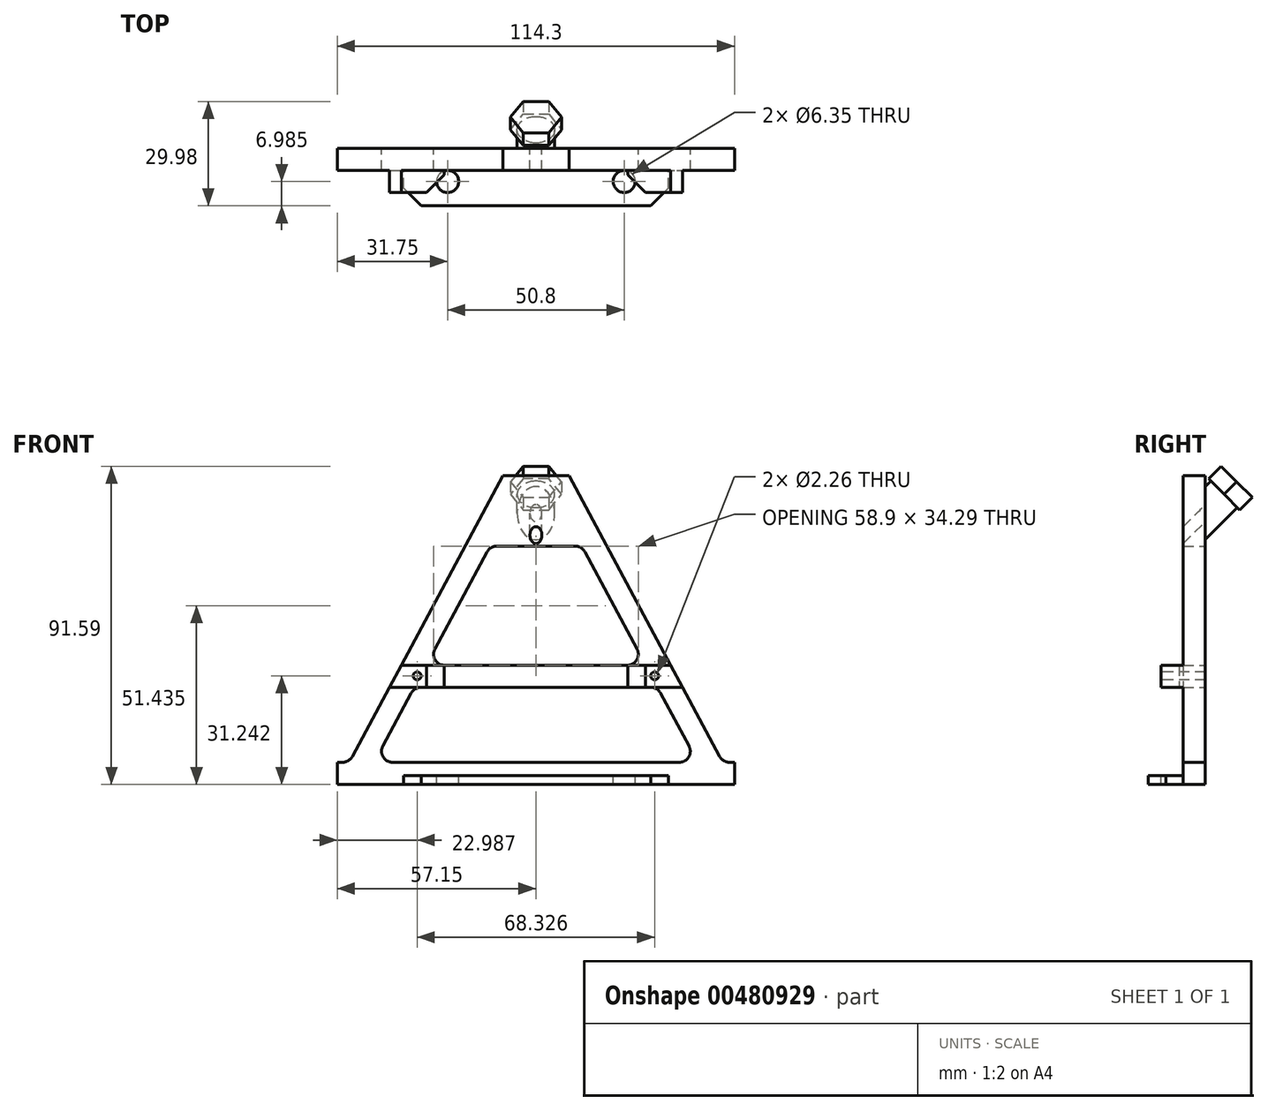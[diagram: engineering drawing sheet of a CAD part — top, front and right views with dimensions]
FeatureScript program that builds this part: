
annotation { "Feature Type Name" : "Feature", "Feature Type Description" : "" }
export const myFeature = defineFeature(function(context is Context, id is Id, definition is map)
    precondition{}
    {
        {
            var Q0;
            Q0=qCreatedBy(makeId("Front.planeOp"),FACE);
            var sketch = newSketch(context, id + "F0", { "sketchPlane" : qUnion([Q0])});
            skLineSegment(sketch, "E0", {"start": v(-9.53, 88.9) * mm, "end": v(9.52, 88.9) * mm});
            skLineSegment(sketch, "E1", {"start": v(-57.15, 0) * mm, "end": v(57.15, 0) * mm});
            skLineSegment(sketch, "E2", {"start": v(57.15, 0) * mm, "end": v(-57.15, 0) * mm});
            skLineSegment(sketch, "E3", {"start": v(-9.52, 88.9) * mm, "end": v(-57.15, 0) * mm});
            skLineSegment(sketch, "E4", {"start": v(9.52, 88.9) * mm, "end": v(57.15, 0) * mm});
            skLineSegment(sketch, "E5", {"start": v(-57.15, 0) * mm, "end": v(-57.15, 6.35) * mm});
            skLineSegment(sketch, "E6", {"start": v(-41.24, 6.35) * mm, "end": v(41.24, 6.35) * mm});
            skLineSegment(sketch, "E7", {"start": v(57.15, 6.35) * mm, "end": v(57.15, 0) * mm});
            skLineSegment(sketch, "E8", {"start": v(-44.04, 11.02) * mm, "end": v(-35.88, 26.26) * mm});
            skLineSegment(sketch, "E9", {"start": v(-11.3, 68.58) * mm, "end": v(11.3, 68.58) * mm});
            skLineSegment(sketch, "E10", {"start": v(35.88, 26.26) * mm, "end": v(44.04, 11.02) * mm});
            skLineSegment(sketch, "E11", {"start": v(-33.08, 27.94) * mm, "end": v(33.08, 27.94) * mm});
            skLineSegment(sketch, "E12", {"start": v(-26.27, 34.3) * mm, "end": v(26.27, 34.3) * mm});
            skArc(sketch, "E13.filletArc", {"start": v(35.88, 26.26) * mm, "mid": v(34.7, 27.49) * mm, "end": v(33.08, 27.94) * mm});
            skArc(sketch, "E14.filletArc", {"start": v(-33.08, 27.94) * mm, "mid": v(-34.7, 27.49) * mm, "end": v(-35.88, 26.26) * mm});
            skArc(sketch, "E15.filletArc", {"start": v(-44.04, 11.02) * mm, "mid": v(-43.97, 7.9) * mm, "end": v(-41.24, 6.35) * mm});
            skPoint(sketch, "E16.newPointA", {"position": v(57.15, 6.35) * mm});
            skArc(sketch, "E16.filletArc", {"start": v(41.24, 6.35) * mm, "mid": v(43.97, 7.9) * mm, "end": v(44.04, 11.02) * mm});
            skLineSegment(sketch, "E17", {"start": v(-29.07, 38.96) * mm, "end": v(-14.1, 66.9) * mm});
            skLineSegment(sketch, "E18", {"start": v(14.1, 66.9) * mm, "end": v(29.07, 38.96) * mm});
            skLineSegment(sketch, "E19", {"start": v(-57.15, 6.35) * mm, "end": v(-53.75, 6.35) * mm});
            skLineSegment(sketch, "E20.trimOffspring", {"start": v(53.75, 6.35) * mm, "end": v(57.15, 6.35) * mm});
            skPoint(sketch, "E21.visualSharp", {"position": v(-31.58, 34.3) * mm});
            skArc(sketch, "E21.filletArc", {"start": v(-29.07, 38.96) * mm, "mid": v(-29, 35.83) * mm, "end": v(-26.27, 34.3) * mm});
            skPoint(sketch, "E22.visualSharp", {"position": v(31.58, 34.3) * mm});
            skArc(sketch, "E22.filletArc", {"start": v(26.27, 34.3) * mm, "mid": v(29, 35.83) * mm, "end": v(29.07, 38.96) * mm});
            skPoint(sketch, "E23.visualSharp", {"position": v(13.2, 68.58) * mm});
            skArc(sketch, "E23.filletArc", {"start": v(14.1, 66.9) * mm, "mid": v(12.94, 68.13) * mm, "end": v(11.3, 68.58) * mm});
            skPoint(sketch, "E24.visualSharp", {"position": v(-13.2, 68.58) * mm});
            skArc(sketch, "E24.filletArc", {"start": v(-11.3, 68.58) * mm, "mid": v(-12.94, 68.13) * mm, "end": v(-14.1, 66.9) * mm});
            skSolve(sketch);
        }
        {
            var Q0;
            Q0 = qSketchRegion(id + "F0", true);
            extrude(context, id + "F1", {"entities" : qUnion([Q0]), "depth" : 6.35 * mm});
        }
        {
            var Q0;
            Q0=makeQuery(id+"F1.opExtrude","SWEPT_EDGE",EDGE,{"disambiguationData":[OSD([sQuery(id+"F0.wireOp",EDGE,"E4"),sQuery(id+"F0.wireOp",EDGE,"E20.trimOffspring")])]});
            var Q1;
            Q1=makeQuery(id+"F1.opExtrude","SWEPT_EDGE",EDGE,{"disambiguationData":[OSD([sQuery(id+"F0.wireOp",EDGE,"E3"),sQuery(id+"F0.wireOp",EDGE,"E19")])]});
            fillet(context, id + "F2", {"entities" : qUnion([Q0, Q1]), "radius" : 3.17 * mm, "tangentPropagation" : true, "allowEdgeOverflow" : false});
        }
        {
            var Q0;
            Q0=makeQuery(id+"F1.opExtrude","CAP_FACE",FACE,{"disambiguationData":[OSD([sQuery(id+"F0.wireOp",EDGE,"E0"),sQuery(id+"F0.wireOp",EDGE,"E2"),sQuery(id+"F0.wireOp",EDGE,"E3"),sQuery(id+"F0.wireOp",EDGE,"E4"),sQuery(id+"F0.wireOp",EDGE,"E5"),sQuery(id+"F0.wireOp",EDGE,"E7"),sQuery(id+"F0.wireOp",EDGE,"E8"),sQuery(id+"F0.wireOp",EDGE,"E9"),sQuery(id+"F0.wireOp",EDGE,"E10"),sQuery(id+"F0.wireOp",EDGE,"E11"),sQuery(id+"F0.wireOp",EDGE,"E12"),sQuery(id+"F0.wireOp",EDGE,"E13.filletArc"),sQuery(id+"F0.wireOp",EDGE,"E14.filletArc"),sQuery(id+"F0.wireOp",EDGE,"E15.filletArc"),sQuery(id+"F0.wireOp",EDGE,"E16.filletArc"),sQuery(id+"F0.wireOp",EDGE,"E17"),sQuery(id+"F0.wireOp",EDGE,"E18"),sQuery(id+"F0.wireOp",EDGE,"E19"),sQuery(id+"F0.wireOp",EDGE,"E6"),sQuery(id+"F0.wireOp",EDGE,"E20.trimOffspring"),sQuery(id+"F0.wireOp",EDGE,"E21.filletArc"),sQuery(id+"F0.wireOp",EDGE,"E22.filletArc"),sQuery(id+"F0.wireOp",EDGE,"E23.filletArc"),sQuery(id+"F0.wireOp",EDGE,"E24.filletArc")])],"isStart":false});
            var sketch = newSketch(context, id + "F3", { "sketchPlane" : qUnion([Q0])});
            skLineSegment(sketch, "E25.bottom", {"start": v(-38.1, 0) * mm, "end": v(38.1, 0) * mm});
            skLineSegment(sketch, "E25.top", {"start": v(-38.1, 2.54) * mm, "end": v(38.1, 2.54) * mm});
            skLineSegment(sketch, "E25.left", {"start": v(-38.1, 0) * mm, "end": v(-38.1, 2.54) * mm});
            skLineSegment(sketch, "E25.right", {"start": v(38.1, 0) * mm, "end": v(38.1, 2.54) * mm});
            skSolve(sketch);
        }
        {
            var Q0;
            Q0 = qSketchRegion(id + "F3", true);
            extrude(context, id + "F4", {"entities" : qUnion([Q0]), "operationType" : NewBodyOperationType.ADD, "depth" : 10.16 * mm});
        }
        {
            var Q0;
            Q0=makeQuery(id+"F4.opExtrude","CAP_EDGE",EDGE,{"disambiguationData":[OSD([sQuery(id+"F3.wireOp",EDGE,"E25.left")])],"isStart":false});
            var Q1;
            Q1=makeQuery(id+"F4.opExtrude","CAP_EDGE",EDGE,{"disambiguationData":[OSD([sQuery(id+"F3.wireOp",EDGE,"E25.right")])],"isStart":false});
            chamfer(context, id + "F5", {"entities" : qUnion([Q0, Q1]), "width" : 5.08 * mm, "tangentPropagation" : true});
        }
        {
            var Q0;
            Q0=makeQuery(id+"F1.opExtrude","CAP_FACE",FACE,{"disambiguationData":[OSD([sQuery(id+"F0.wireOp",EDGE,"E0"),sQuery(id+"F0.wireOp",EDGE,"E2"),sQuery(id+"F0.wireOp",EDGE,"E3"),sQuery(id+"F0.wireOp",EDGE,"E4"),sQuery(id+"F0.wireOp",EDGE,"E5"),sQuery(id+"F0.wireOp",EDGE,"E7"),sQuery(id+"F0.wireOp",EDGE,"E8"),sQuery(id+"F0.wireOp",EDGE,"E9"),sQuery(id+"F0.wireOp",EDGE,"E10"),sQuery(id+"F0.wireOp",EDGE,"E11"),sQuery(id+"F0.wireOp",EDGE,"E12"),sQuery(id+"F0.wireOp",EDGE,"E13.filletArc"),sQuery(id+"F0.wireOp",EDGE,"E14.filletArc"),sQuery(id+"F0.wireOp",EDGE,"E15.filletArc"),sQuery(id+"F0.wireOp",EDGE,"E16.filletArc"),sQuery(id+"F0.wireOp",EDGE,"E17"),sQuery(id+"F0.wireOp",EDGE,"E18"),sQuery(id+"F0.wireOp",EDGE,"E19"),sQuery(id+"F0.wireOp",EDGE,"E6"),sQuery(id+"F0.wireOp",EDGE,"E20.trimOffspring"),sQuery(id+"F0.wireOp",EDGE,"E21.filletArc"),sQuery(id+"F0.wireOp",EDGE,"E22.filletArc"),sQuery(id+"F0.wireOp",EDGE,"E23.filletArc"),sQuery(id+"F0.wireOp",EDGE,"E24.filletArc")])],"isStart":false});
            var sketch = newSketch(context, id + "F6", { "sketchPlane" : qUnion([Q0])});
            skLineSegment(sketch, "E26.0", {"start": v(-33.08, 27.94) * mm, "end": v(33.08, 27.94) * mm});
            skLineSegment(sketch, "E27.0", {"start": v(-26.27, 34.3) * mm, "end": v(26.27, 34.3) * mm});
            skLineSegment(sketch, "E28", {"start": v(26.27, 34.3) * mm, "end": v(38.78, 34.3) * mm});
            skLineSegment(sketch, "E29", {"start": v(33.08, 27.94) * mm, "end": v(42.18, 27.94) * mm});
            skLineSegment(sketch, "E30", {"start": v(-26.27, 34.3) * mm, "end": v(-38.78, 34.3) * mm});
            skLineSegment(sketch, "E31", {"start": v(-42.18, 27.94) * mm, "end": v(-33.08, 27.94) * mm});
            skLineSegment(sketch, "E32", {"start": v(-42.18, 27.94) * mm, "end": v(-38.78, 34.3) * mm});
            skLineSegment(sketch, "E33", {"start": v(42.18, 27.94) * mm, "end": v(38.78, 34.3) * mm});
            skLineSegment(sketch, "E34", {"start": v(26.43, 34.3) * mm, "end": v(26.43, 27.94) * mm});
            skLineSegment(sketch, "E35", {"start": v(-26.43, 34.3) * mm, "end": v(-26.43, 27.94) * mm});
            skSolve(sketch);
        }
        {
            var Q0;
            {var subQ0=sQuery(id+"F6.wireOp",EDGE,"E31");Q0=makeQuery(id+"F6.imprint","IMPRINT",FACE,{"disambiguationData":[TD([[makeQuery(id+"F6.imprint","IMPRINT",EDGE,{"derivedFrom":subQ0}),1.0]])]});}
            var Q1;
            {var subQ1=sQuery(id+"F6.wireOp",EDGE,"E29");Q1=makeQuery(id+"F6.imprint","IMPRINT",FACE,{"disambiguationData":[TD([[makeQuery(id+"F6.imprint","IMPRINT",EDGE,{"derivedFrom":subQ1}),1.0]])]});}
            extrude(context, id + "F7", {"entities" : qUnion([Q0, Q1]), "operationType" : NewBodyOperationType.ADD, "depth" : 6.35 * mm});
        }
        {
            var Q0;
            Q0=makeQuery(id+"F7.opExtrude","CAP_EDGE",EDGE,{"disambiguationData":[OSD([sQuery(id+"F6.wireOp",EDGE,"E34")])],"isStart":false});
            var Q1;
            Q1=makeQuery(id+"F7.opExtrude","CAP_EDGE",EDGE,{"disambiguationData":[OSD([sQuery(id+"F6.wireOp",EDGE,"E35")])],"isStart":false});
            chamfer(context, id + "F8", {"entities" : qUnion([Q0, Q1]), "width" : 5.08 * mm, "tangentPropagation" : true});
        }
        {
            var Q0;
            Q0=makeQuery(id+"F7.opExtrude","CAP_FACE",FACE,{"disambiguationData":[OSD([sQuery(id+"F6.wireOp",EDGE,"E26.0"),sQuery(id+"F6.wireOp",EDGE,"E28"),sQuery(id+"F6.wireOp",EDGE,"E29"),sQuery(id+"F6.wireOp",EDGE,"E33"),sQuery(id+"F6.wireOp",EDGE,"E34")])],"isStart":false});
            var sketch = newSketch(context, id + "F9", { "sketchPlane" : qUnion([Q0])});
            skPoint(sketch, "E36", {"position": v(34.16, 31.24) * mm});
            skPoint(sketch, "E37", {"position": v(-34.16, 31.24) * mm});
            skSolve(sketch);
        }
        {
            var Q0;
            Q0=sQuery(id+"F9.wireOp",VERTEX,"E37");
            var Q1;
            Q1=sQuery(id+"F9.wireOp",VERTEX,"E36");
            var Q2;
            Q2=makeQuery(id+"F1.opExtrude","SWEPT_BODY",BODY,{"disambiguationData":[OSD([sQuery(id+"F0.wireOp",EDGE,"E0"),sQuery(id+"F0.wireOp",EDGE,"E2"),sQuery(id+"F0.wireOp",EDGE,"E3"),sQuery(id+"F0.wireOp",EDGE,"E4"),sQuery(id+"F0.wireOp",EDGE,"E5"),sQuery(id+"F0.wireOp",EDGE,"E7"),sQuery(id+"F0.wireOp",EDGE,"E8"),sQuery(id+"F0.wireOp",EDGE,"E9"),sQuery(id+"F0.wireOp",EDGE,"E10"),sQuery(id+"F0.wireOp",EDGE,"E11"),sQuery(id+"F0.wireOp",EDGE,"E12"),sQuery(id+"F0.wireOp",EDGE,"E13.filletArc"),sQuery(id+"F0.wireOp",EDGE,"E14.filletArc"),sQuery(id+"F0.wireOp",EDGE,"E15.filletArc"),sQuery(id+"F0.wireOp",EDGE,"E16.filletArc"),sQuery(id+"F0.wireOp",EDGE,"E17"),sQuery(id+"F0.wireOp",EDGE,"E18"),sQuery(id+"F0.wireOp",EDGE,"E19"),sQuery(id+"F0.wireOp",EDGE,"E6"),sQuery(id+"F0.wireOp",EDGE,"E20.trimOffspring"),sQuery(id+"F0.wireOp",EDGE,"E21.filletArc"),sQuery(id+"F0.wireOp",EDGE,"E22.filletArc"),sQuery(id+"F0.wireOp",EDGE,"E23.filletArc"),sQuery(id+"F0.wireOp",EDGE,"E24.filletArc")])]});
            hole(context, id + "F10", {"style" : HoleStyle.SIMPLE, "endStyle" : HoleEndStyle.THROUGH, "standardTappedOrClearance" : lookupTablePath({ "standard" : "ANSI", "fit" : "Normal (ASME)", "engagement" : "75%", "pitch" : "40 tpi", "size" : "#4", "type" : "Tapped" }), "standardBlindInLast" : lookupTablePath({ "fit" : "Free", "standard" : "ANSI", "engagement" : "75%", "pitch" : "40 tpi", "size" : "#4", "type" : "Tapped" }), "holeDiameter" : 2.26 * mm, "showTappedDepth" : true, "tappedDepth" : 6.35 * mm, "tapClearance" : 3, "locations" : qUnion([Q0, Q1]), "scope" : qUnion([Q2]), "majorDiameter" : 2.84 * mm});
        }
        {
            var Q0;
            Q0=makeQuery(id+"F1.opExtrude","CAP_EDGE",EDGE,{"disambiguationData":[OSD([sQuery(id+"F0.wireOp",EDGE,"E0")])],"isStart":true});
            cPlane(context, id + "F11", {"entities" : qUnion([Q0]), "cplaneType" : CPlaneType.LINE_ANGLE, "offset" : 25.4 * mm, "angle" : 45 * degree, "width" : 152.4 * mm, "height" : 152.4 * mm});
        }
        {
            var Q0;
            Q0=qCreatedBy(id+"F11.planeOp",FACE);
            var sketch = newSketch(context, id + "F12", { "sketchPlane" : qUnion([Q0])});
            skCircle(sketch, "E38.cCircle", {"center": v(0, 55.24) * mm, "radius": 6.35 * mm, "construction": true});
            skLineSegment(sketch, "E38.0", {"start": v(3.67, 48.9) * mm, "end": v(-3.67, 48.9) * mm});
            skLineSegment(sketch, "E38.1", {"start": v(-3.67, 48.9) * mm, "end": v(-7.33, 55.24) * mm});
            skLineSegment(sketch, "E38.2", {"start": v(-7.33, 55.24) * mm, "end": v(-3.67, 61.6) * mm});
            skLineSegment(sketch, "E38.3", {"start": v(-3.67, 61.6) * mm, "end": v(3.67, 61.6) * mm});
            skLineSegment(sketch, "E38.4", {"start": v(3.67, 61.6) * mm, "end": v(7.33, 55.24) * mm});
            skLineSegment(sketch, "E38.5", {"start": v(7.33, 55.24) * mm, "end": v(3.67, 48.9) * mm});
            skPoint(sketch, "E38.0.midPoint", {"position": v(0, 48.9) * mm});
            skSolve(sketch);
        }
        {
            var Q0;
            Q0 = qSketchRegion(id + "F12", true);
            extrude(context, id + "F13", {"entities" : qUnion([Q0]), "depth" : 5.08 * mm});
        }
        {
            var Q0;
            Q0=makeQuery(id+"F13.opExtrude","CAP_FACE",FACE,{"disambiguationData":[OSD([sQuery(id+"F12.wireOp",EDGE,"E38.0"),sQuery(id+"F12.wireOp",EDGE,"E38.1"),sQuery(id+"F12.wireOp",EDGE,"E38.2"),sQuery(id+"F12.wireOp",EDGE,"E38.3"),sQuery(id+"F12.wireOp",EDGE,"E38.4"),sQuery(id+"F12.wireOp",EDGE,"E38.5")])],"isStart":true});
            var sketch = newSketch(context, id + "F14", { "sketchPlane" : qUnion([Q0])});
            skCircle(sketch, "E39", {"center": v(0, 55.24) * mm, "radius": 5.4 * mm});
            skSolve(sketch);
        }
        {
            var Q0;
            Q0 = qSketchRegion(id + "F14", true);
            var Q1;
            Q1=makeQuery(id+"F1.opExtrude","CAP_FACE",FACE,{"disambiguationData":[OSD([sQuery(id+"F0.wireOp",EDGE,"E0"),sQuery(id+"F0.wireOp",EDGE,"E2"),sQuery(id+"F0.wireOp",EDGE,"E3"),sQuery(id+"F0.wireOp",EDGE,"E4"),sQuery(id+"F0.wireOp",EDGE,"E5"),sQuery(id+"F0.wireOp",EDGE,"E7"),sQuery(id+"F0.wireOp",EDGE,"E8"),sQuery(id+"F0.wireOp",EDGE,"E9"),sQuery(id+"F0.wireOp",EDGE,"E10"),sQuery(id+"F0.wireOp",EDGE,"E11"),sQuery(id+"F0.wireOp",EDGE,"E12"),sQuery(id+"F0.wireOp",EDGE,"E13.filletArc"),sQuery(id+"F0.wireOp",EDGE,"E14.filletArc"),sQuery(id+"F0.wireOp",EDGE,"E15.filletArc"),sQuery(id+"F0.wireOp",EDGE,"E16.filletArc"),sQuery(id+"F0.wireOp",EDGE,"E17"),sQuery(id+"F0.wireOp",EDGE,"E18"),sQuery(id+"F0.wireOp",EDGE,"E19"),sQuery(id+"F0.wireOp",EDGE,"E6"),sQuery(id+"F0.wireOp",EDGE,"E20.trimOffspring"),sQuery(id+"F0.wireOp",EDGE,"E21.filletArc"),sQuery(id+"F0.wireOp",EDGE,"E22.filletArc"),sQuery(id+"F0.wireOp",EDGE,"E23.filletArc"),sQuery(id+"F0.wireOp",EDGE,"E24.filletArc")])],"isStart":true});
            extrude(context, id + "F15", {"entities" : qUnion([Q0]), "endBound" : BoundingType.UP_TO_SURFACE, "endBoundEntityFace" : qUnion([Q1]), "depth" : 25.4 * mm});
        }
        {
            var Q0;
            Q0=makeQuery(id+"F13.opExtrude","CAP_FACE",FACE,{"disambiguationData":[OSD([sQuery(id+"F12.wireOp",EDGE,"E38.0"),sQuery(id+"F12.wireOp",EDGE,"E38.1"),sQuery(id+"F12.wireOp",EDGE,"E38.2"),sQuery(id+"F12.wireOp",EDGE,"E38.3"),sQuery(id+"F12.wireOp",EDGE,"E38.4"),sQuery(id+"F12.wireOp",EDGE,"E38.5")])],"isStart":false});
            var sketch = newSketch(context, id + "F16", { "sketchPlane" : qUnion([Q0])});
            skPoint(sketch, "E40", {"position": v(0, 55.24) * mm});
            skSolve(sketch);
        }
        {
            var Q0;
            Q0=sQuery(id+"F16.wireOp",VERTEX,"E40");
            var Q1;
            Q1=makeQuery(id+"F1.opExtrude","SWEPT_BODY",BODY,{"disambiguationData":[OSD([sQuery(id+"F0.wireOp",EDGE,"E0"),sQuery(id+"F0.wireOp",EDGE,"E2"),sQuery(id+"F0.wireOp",EDGE,"E3"),sQuery(id+"F0.wireOp",EDGE,"E4"),sQuery(id+"F0.wireOp",EDGE,"E5"),sQuery(id+"F0.wireOp",EDGE,"E7"),sQuery(id+"F0.wireOp",EDGE,"E8"),sQuery(id+"F0.wireOp",EDGE,"E9"),sQuery(id+"F0.wireOp",EDGE,"E10"),sQuery(id+"F0.wireOp",EDGE,"E11"),sQuery(id+"F0.wireOp",EDGE,"E12"),sQuery(id+"F0.wireOp",EDGE,"E13.filletArc"),sQuery(id+"F0.wireOp",EDGE,"E14.filletArc"),sQuery(id+"F0.wireOp",EDGE,"E15.filletArc"),sQuery(id+"F0.wireOp",EDGE,"E16.filletArc"),sQuery(id+"F0.wireOp",EDGE,"E17"),sQuery(id+"F0.wireOp",EDGE,"E18"),sQuery(id+"F0.wireOp",EDGE,"E19"),sQuery(id+"F0.wireOp",EDGE,"E6"),sQuery(id+"F0.wireOp",EDGE,"E20.trimOffspring"),sQuery(id+"F0.wireOp",EDGE,"E21.filletArc"),sQuery(id+"F0.wireOp",EDGE,"E22.filletArc"),sQuery(id+"F0.wireOp",EDGE,"E23.filletArc"),sQuery(id+"F0.wireOp",EDGE,"E24.filletArc")])]});
            hole(context, id + "F17", {"style" : HoleStyle.SIMPLE, "endStyle" : HoleEndStyle.THROUGH, "standardTappedOrClearance" : lookupTablePath({ "standard" : "ANSI", "fit" : "Normal (ASME)", "engagement" : "75%", "pitch" : "32 tpi", "size" : "#8", "type" : "Tapped" }), "standardBlindInLast" : lookupTablePath({ "fit" : "Free", "standard" : "ANSI", "engagement" : "75%", "pitch" : "32 tpi", "size" : "#8", "type" : "Tapped" }), "holeDiameter" : 3.45 * mm, "showTappedDepth" : true, "tappedDepth" : 6.35 * mm, "tapClearance" : 3, "locations" : qUnion([Q0]), "scope" : qUnion([Q1]), "majorDiameter" : 4.17 * mm});
        }
        {
            var Q0;
            Q0=makeQuery(id+"F4.opExtrude","SWEPT_FACE",FACE,{"disambiguationData":[OSD([sQuery(id+"F3.wireOp",EDGE,"E25.top")])]});
            var sketch = newSketch(context, id + "F18", { "sketchPlane" : qUnion([Q0])});
            skPoint(sketch, "E41", {"position": v(-25.4, -9.53) * mm});
            skPoint(sketch, "E42", {"position": v(25.4, -9.52) * mm});
            skSolve(sketch);
        }
        {
            var Q0;
            Q0=sQuery(id+"F18.wireOp",VERTEX,"E41");
            var Q1;
            Q1=sQuery(id+"F18.wireOp",VERTEX,"E42");
            var Q2;
            Q2=makeQuery(id+"F1.opExtrude","SWEPT_BODY",BODY,{"disambiguationData":[OSD([sQuery(id+"F0.wireOp",EDGE,"E0"),sQuery(id+"F0.wireOp",EDGE,"E2"),sQuery(id+"F0.wireOp",EDGE,"E3"),sQuery(id+"F0.wireOp",EDGE,"E4"),sQuery(id+"F0.wireOp",EDGE,"E5"),sQuery(id+"F0.wireOp",EDGE,"E7"),sQuery(id+"F0.wireOp",EDGE,"E8"),sQuery(id+"F0.wireOp",EDGE,"E9"),sQuery(id+"F0.wireOp",EDGE,"E10"),sQuery(id+"F0.wireOp",EDGE,"E11"),sQuery(id+"F0.wireOp",EDGE,"E12"),sQuery(id+"F0.wireOp",EDGE,"E13.filletArc"),sQuery(id+"F0.wireOp",EDGE,"E14.filletArc"),sQuery(id+"F0.wireOp",EDGE,"E15.filletArc"),sQuery(id+"F0.wireOp",EDGE,"E16.filletArc"),sQuery(id+"F0.wireOp",EDGE,"E17"),sQuery(id+"F0.wireOp",EDGE,"E18"),sQuery(id+"F0.wireOp",EDGE,"E19"),sQuery(id+"F0.wireOp",EDGE,"E6"),sQuery(id+"F0.wireOp",EDGE,"E20.trimOffspring"),sQuery(id+"F0.wireOp",EDGE,"E21.filletArc"),sQuery(id+"F0.wireOp",EDGE,"E22.filletArc"),sQuery(id+"F0.wireOp",EDGE,"E23.filletArc"),sQuery(id+"F0.wireOp",EDGE,"E24.filletArc")])]});
            hole(context, id + "F19", {"style" : HoleStyle.SIMPLE, "endStyle" : HoleEndStyle.THROUGH, "holeDiameter" : 6.35 * mm, "isTappedThrough" : true, "tappedDepth" : 12.7 * mm, "tapClearance" : 3, "locations" : qUnion([Q0, Q1]), "scope" : qUnion([Q2])});
        }
    });
